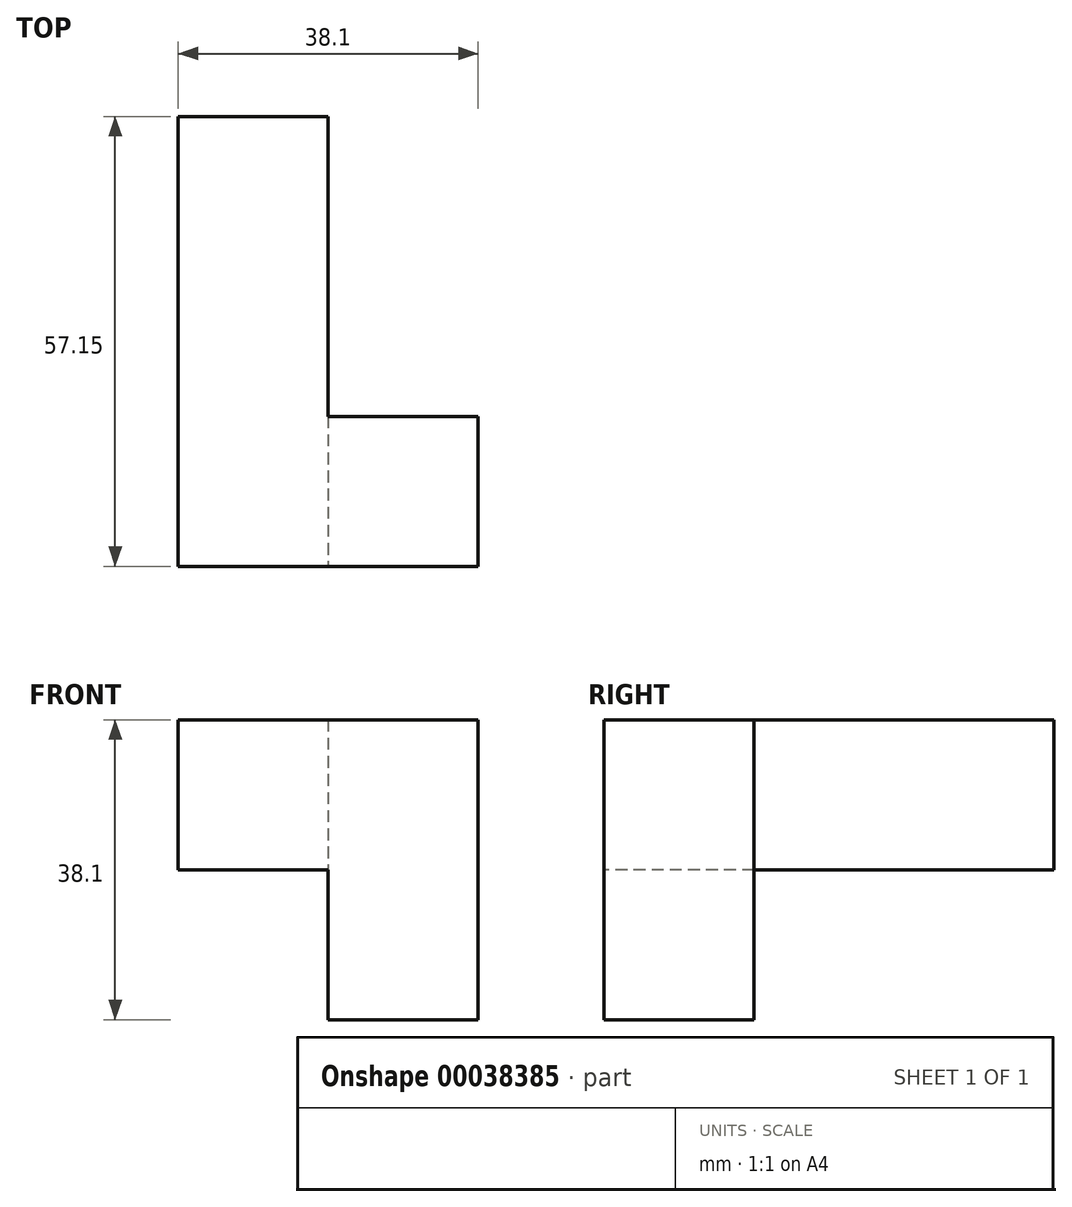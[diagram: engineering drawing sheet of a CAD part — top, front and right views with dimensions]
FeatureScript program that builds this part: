
annotation { "Feature Type Name" : "Feature", "Feature Type Description" : "" }
export const myFeature = defineFeature(function(context is Context, id is Id, definition is map)
    precondition{}
    {
        {
            var Q0;
            Q0=qCreatedBy(makeId("Top.planeOp"),FACE);
            var sketch = newSketch(context, id + "F0", { "sketchPlane" : qUnion([Q0])});
            skLineSegment(sketch, "E0.bottom", {"start": v(0, 0) * mm, "end": v(19.05, 0) * mm});
            skLineSegment(sketch, "E0.top", {"start": v(0, 19.05) * mm, "end": v(19.05, 19.05) * mm});
            skLineSegment(sketch, "E0.left", {"start": v(0, 0) * mm, "end": v(0, 19.05) * mm});
            skLineSegment(sketch, "E0.right", {"start": v(19.05, 0) * mm, "end": v(19.05, 19.05) * mm});
            skSolve(sketch);
        }
        {
            var Q0;
            Q0=makeQuery(id+"F0.imprint","IMPRINT",FACE,{"disambiguationData":[TD([[makeQuery(id+"F0.imprint","IMPRINT",EDGE,{"derivedFrom":sQuery(id+"F0.wireOp",EDGE,"E0.bottom")}),1.0]])]});
            extrude(context, id + "F1", {"entities" : qUnion([Q0]), "depth" : 19.05 * mm});
        }
        {
            var Q0;
            Q0=makeQuery(id+"F1.opExtrude","CAP_FACE",FACE,{"disambiguationData":[OSD([sQuery(id+"F0.wireOp",EDGE,"E0.bottom"),sQuery(id+"F0.wireOp",EDGE,"E0.top"),sQuery(id+"F0.wireOp",EDGE,"E0.left"),sQuery(id+"F0.wireOp",EDGE,"E0.right")])],"isStart":false});
            extrude(context, id + "F2", {"entities" : qUnion([Q0]), "operationType" : NewBodyOperationType.ADD, "depth" : 19.05 * mm});
        }
        {
            var Q0;
            {var subQ0=sQuery(id+"F0.wireOp",EDGE,"E0.left");Q0=makeQuery(id+"F2.boolean.opBoolean","MERGE",FACE,{"derivedFrom":[makeQuery(id+"F1.opExtrude","SWEPT_FACE",FACE,{"disambiguationData":[OSD([subQ0])]}),makeQuery(id+"F2.opExtrude","SWEPT_FACE",FACE,{"disambiguationData":[OSD([subQ0])]})]});}
            var sketch = newSketch(context, id + "F3", { "sketchPlane" : qUnion([Q0])});
            skLineSegment(sketch, "E1.bottom", {"start": v(-19.05, 38.1) * mm, "end": v(0, 38.1) * mm});
            skLineSegment(sketch, "E1.top", {"start": v(-19.05, 19.05) * mm, "end": v(0, 19.05) * mm});
            skLineSegment(sketch, "E1.left", {"start": v(-19.05, 38.1) * mm, "end": v(-19.05, 19.05) * mm});
            skLineSegment(sketch, "E1.right", {"start": v(0, 38.1) * mm, "end": v(0, 19.05) * mm});
            skLineSegment(sketch, "E2.bottom", {"start": v(0, 19.05) * mm, "end": v(-19.05, 19.05) * mm});
            skLineSegment(sketch, "E2.top", {"start": v(0, 0) * mm, "end": v(-19.05, 0) * mm});
            skLineSegment(sketch, "E2.left", {"start": v(0, 19.05) * mm, "end": v(0, 0) * mm});
            skLineSegment(sketch, "E2.right", {"start": v(-19.05, 19.05) * mm, "end": v(-19.05, 0) * mm});
            skSolve(sketch);
        }
        {
            var Q0;
            Q0=makeQuery(id+"F3.imprint","IMPRINT",FACE,{"disambiguationData":[TD([[makeQuery(id+"F3.imprint","IMPRINT",EDGE,{"derivedFrom":sQuery(id+"F3.wireOp",EDGE,"E1.bottom")}),1.0]])]});
            extrude(context, id + "F4", {"entities" : qUnion([Q0]), "operationType" : NewBodyOperationType.ADD, "depth" : 19.05 * mm});
        }
        {
            var Q0;
            {var subQ0=sQuery(id+"F0.wireOp",EDGE,"E0.top");Q0=makeQuery(id+"F4.boolean.opBoolean","MERGE",FACE,{"derivedFrom":[makeQuery(id+"F2.boolean.opBoolean","MERGE",FACE,{"derivedFrom":[makeQuery(id+"F1.opExtrude","SWEPT_FACE",FACE,{"disambiguationData":[OSD([subQ0])]}),makeQuery(id+"F2.opExtrude","SWEPT_FACE",FACE,{"disambiguationData":[OSD([subQ0])]})]}),makeQuery(id+"F4.opExtrude","SWEPT_FACE",FACE,{"disambiguationData":[OSD([sQuery(id+"F3.wireOp",EDGE,"E1.left")])]})]});}
            var sketch = newSketch(context, id + "F5", { "sketchPlane" : qUnion([Q0])});
            skLineSegment(sketch, "E3.bottom", {"start": v(19.05, 38.1) * mm, "end": v(0, 38.1) * mm});
            skLineSegment(sketch, "E3.top", {"start": v(19.05, 19.05) * mm, "end": v(0, 19.05) * mm});
            skLineSegment(sketch, "E3.left", {"start": v(19.05, 38.1) * mm, "end": v(19.05, 19.05) * mm});
            skLineSegment(sketch, "E3.right", {"start": v(0, 38.1) * mm, "end": v(0, 19.05) * mm});
            skSolve(sketch);
        }
        {
            var Q0;
            Q0=makeQuery(id+"F5.imprint","IMPRINT",FACE,{"disambiguationData":[TD([[makeQuery(id+"F5.imprint","IMPRINT",EDGE,{"derivedFrom":sQuery(id+"F5.wireOp",EDGE,"E3.bottom")}),1.0]])]});
            extrude(context, id + "F6", {"entities" : qUnion([Q0]), "operationType" : NewBodyOperationType.ADD, "depth" : 19.05 * mm});
        }
        {
            var Q0;
            Q0=makeQuery(id+"F6.opExtrude","CAP_FACE",FACE,{"disambiguationData":[OSD([sQuery(id+"F5.wireOp",EDGE,"E3.bottom"),sQuery(id+"F5.wireOp",EDGE,"E3.top"),sQuery(id+"F5.wireOp",EDGE,"E3.left"),sQuery(id+"F5.wireOp",EDGE,"E3.right")])],"isStart":false});
            extrude(context, id + "F7", {"entities" : qUnion([Q0]), "operationType" : NewBodyOperationType.ADD, "depth" : 19.05 * mm});
        }
    });
